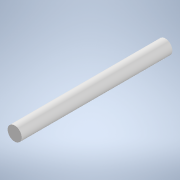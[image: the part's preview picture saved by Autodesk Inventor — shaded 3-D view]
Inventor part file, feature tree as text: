
AUTODESK INVENTOR PART (.ipt)
format: ipt  version: 2022 (Build 260153000, 153)  size: 91,648 bytes
history: native  units: mm
features: other x3, extrude x1, sketch x1, reference x1
ambient origin geometry x8: Origin, YZ Plane, XZ Plane, XY Plane, X Axis, Y Axis, Z Axis, Center Point
bodies: Solid1 (feature_tree)
feature tree (6):
  extrude  "Extrusion1"  [1 undecoded]
  sketch  "Sketch1"  dims[d0=64.238mm d1=0.0mm]
  reference  "Reference1"
  other  "<userpath>\Documents\Inventor\etchasketch\Knobass.iam"
  other  "Knobass.iam"
  other  "knob:1"
note: 1 required parameter value undecoded (feature->parameter linkage not recoverable at this tier; creation-order binding heuristic only, values carry confidence <= 0.55)
